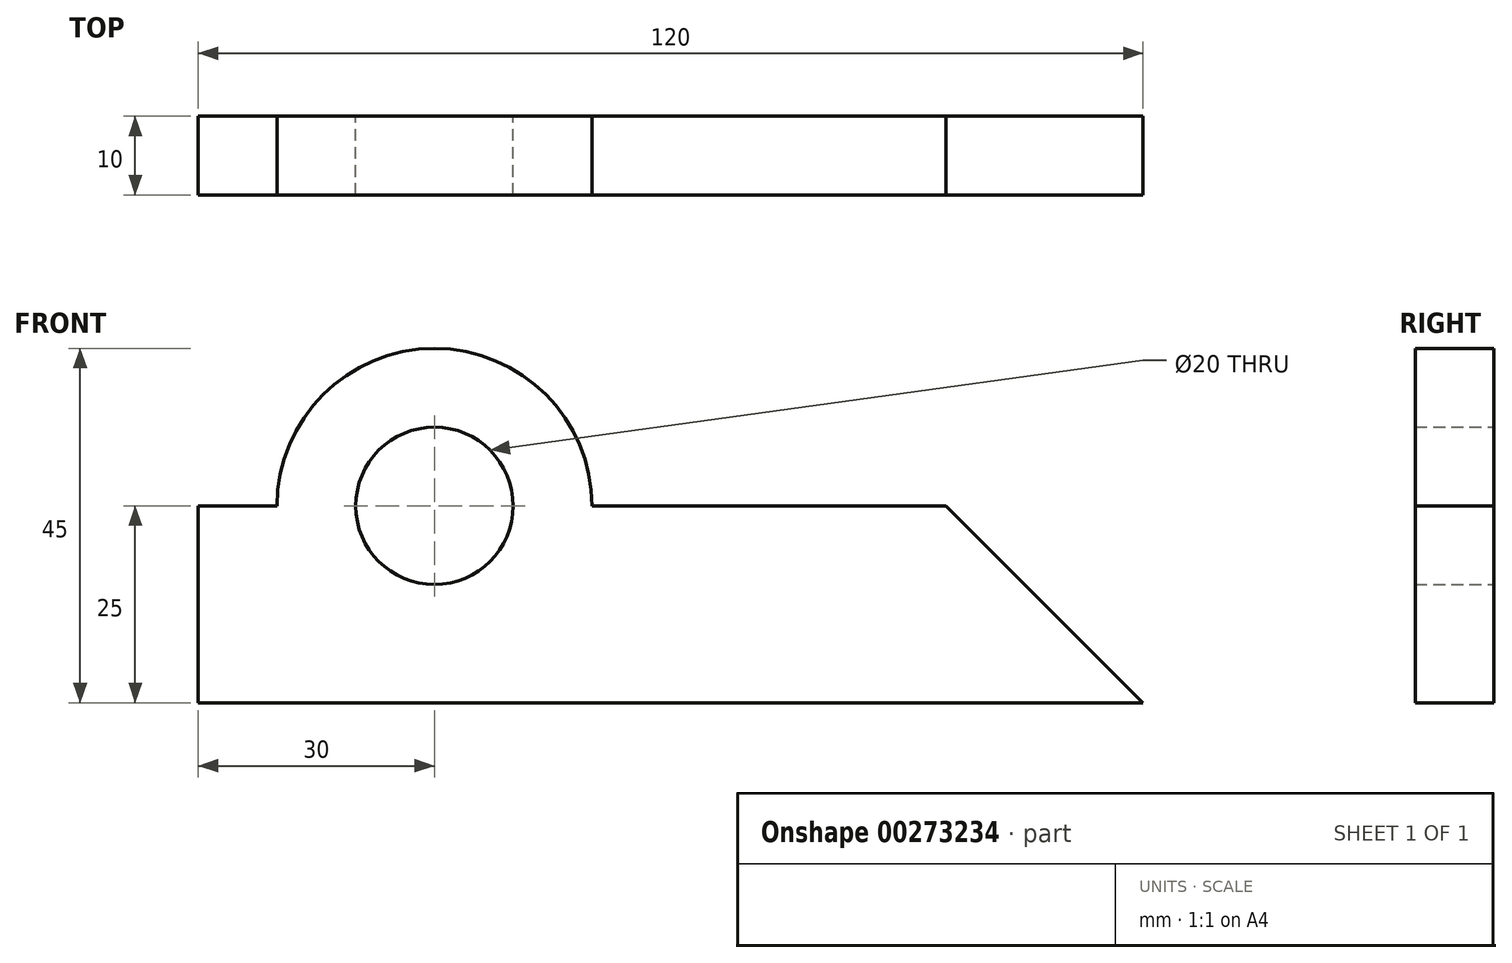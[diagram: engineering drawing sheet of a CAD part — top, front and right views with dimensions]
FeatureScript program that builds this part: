
annotation { "Feature Type Name" : "Feature", "Feature Type Description" : "" }
export const myFeature = defineFeature(function(context is Context, id is Id, definition is map)
    precondition{}
    {
        {
            var Q0;
            Q0=qCreatedBy(makeId("Front.planeOp"),FACE);
            var sketch = newSketch(context, id + "F0", { "sketchPlane" : qUnion([Q0])});
            skLineSegment(sketch, "E0", {"start": v(0, 0) * mm, "end": v(0, 25) * mm});
            skLineSegment(sketch, "E1", {"start": v(0, 0) * mm, "end": v(120, 0) * mm});
            skCircle(sketch, "E2", {"center": v(30, 25) * mm, "radius": 10 * mm});
            skLineSegment(sketch, "E3", {"start": v(0, 25) * mm, "end": v(10, 25) * mm});
            skLineSegment(sketch, "E4", {"start": v(120, 0) * mm, "end": v(95, 25) * mm});
            skLineSegment(sketch, "E5", {"start": v(95, 25) * mm, "end": v(50, 25) * mm});
            skArc(sketch, "E6", {"start": v(50, 25) * mm, "mid": v(30, 45) * mm, "end": v(10, 25) * mm});
            skSolve(sketch);
        }
        {
            var Q0;
            Q0=makeQuery(id+"F0.imprint","IMPRINT",FACE,{"disambiguationData":[TD([[makeQuery(id+"F0.imprint","IMPRINT",EDGE,{"derivedFrom":sQuery(id+"F0.wireOp",EDGE,"E0")}),-1.0]])]});
            extrude(context, id + "F1", {"entities" : qUnion([Q0]), "depth" : 10 * mm});
        }
    });
